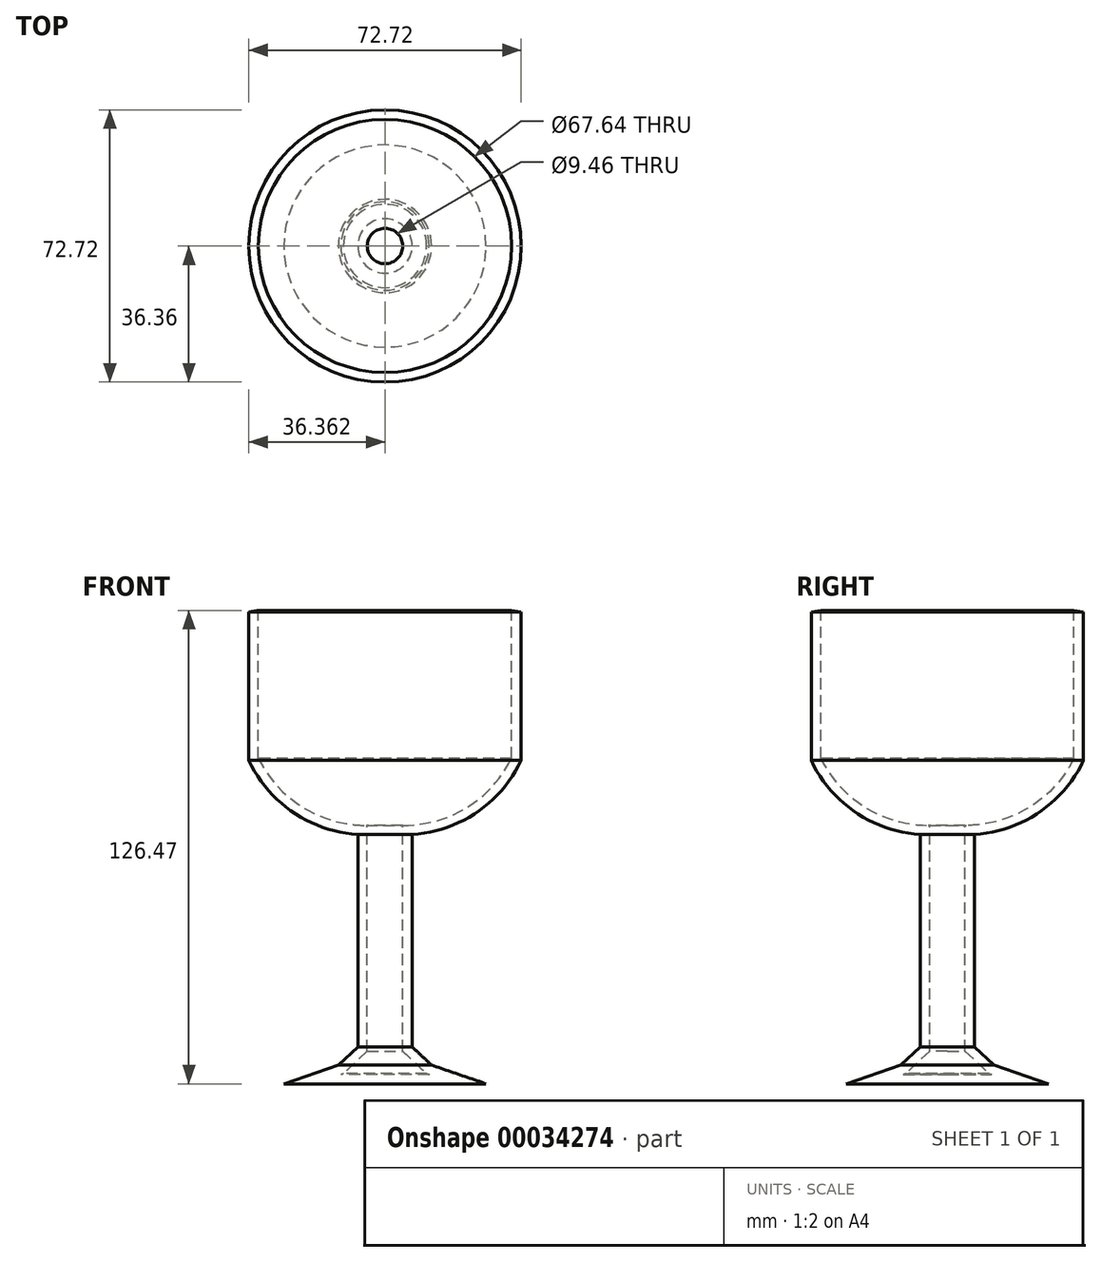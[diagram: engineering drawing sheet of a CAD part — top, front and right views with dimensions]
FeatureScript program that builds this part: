
annotation { "Feature Type Name" : "Feature", "Feature Type Description" : "" }
export const myFeature = defineFeature(function(context is Context, id is Id, definition is map)
    precondition{}
    {
        {
            var Q0;
            Q0=qCreatedBy(makeId("Front.planeOp"),FACE);
            var sketch = newSketch(context, id + "F0", { "sketchPlane" : qUnion([Q0])});
            skLineSegment(sketch, "E0", {"start": v(0, 0) * mm, "end": v(-19.74, 0) * mm});
            skLineSegment(sketch, "E1", {"start": v(-19.74, 0) * mm, "end": v(-5.2, 5) * mm});
            skLineSegment(sketch, "E2", {"start": v(-5.2, 5) * mm, "end": v(0, 9.83) * mm});
            skLineSegment(sketch, "E3", {"start": v(0, 9.83) * mm, "end": v(0, 66.6) * mm});
            skArc(sketch, "E4", {"start": v(-29.09, 86.4) * mm, "mid": v(-17.25, 72.53) * mm, "end": v(0, 66.6) * mm});
            skLineSegment(sketch, "E5", {"start": v(-29.09, 86.4) * mm, "end": v(-29.09, 126.03) * mm});
            skLineSegment(sketch, "E6", {"start": v(-29.09, 126.03) * mm, "end": v(7.27, 132.22) * mm});
            skLineSegment(sketch, "E7", {"start": v(7.27, 132.22) * mm, "end": v(7.27, 0) * mm});
            skLineSegment(sketch, "E8", {"start": v(7.27, 0) * mm, "end": v(0, 0) * mm});
            skSolve(sketch);
        }
        {
            var Q0;
            Q0=makeQuery(id+"F0.imprint","IMPRINT",FACE,{"disambiguationData":[TD([[makeQuery(id+"F0.imprint","IMPRINT",EDGE,{"derivedFrom":sQuery(id+"F0.wireOp",EDGE,"E0")}),-1.0]])]});
            var Q1;
            Q1=sQuery(id+"F0.wireOp",EDGE,"E7");
            revolve(context, id + "F1", {"entities" : qUnion([Q0]), "axis" : qUnion([Q1]), "revolveType" : RevolveType.FULL});
        }
        {
            var Q0;
            Q0=makeQuery(id+"F1.opRevolve","SWEPT_FACE",FACE,{"disambiguationData":[OSD([sQuery(id+"F0.wireOp",EDGE,"E6")])]});
            shell(context, id + "F2", {"entities" : qUnion([Q0]), "thickness" : 2.54 * mm});
        }
    });
